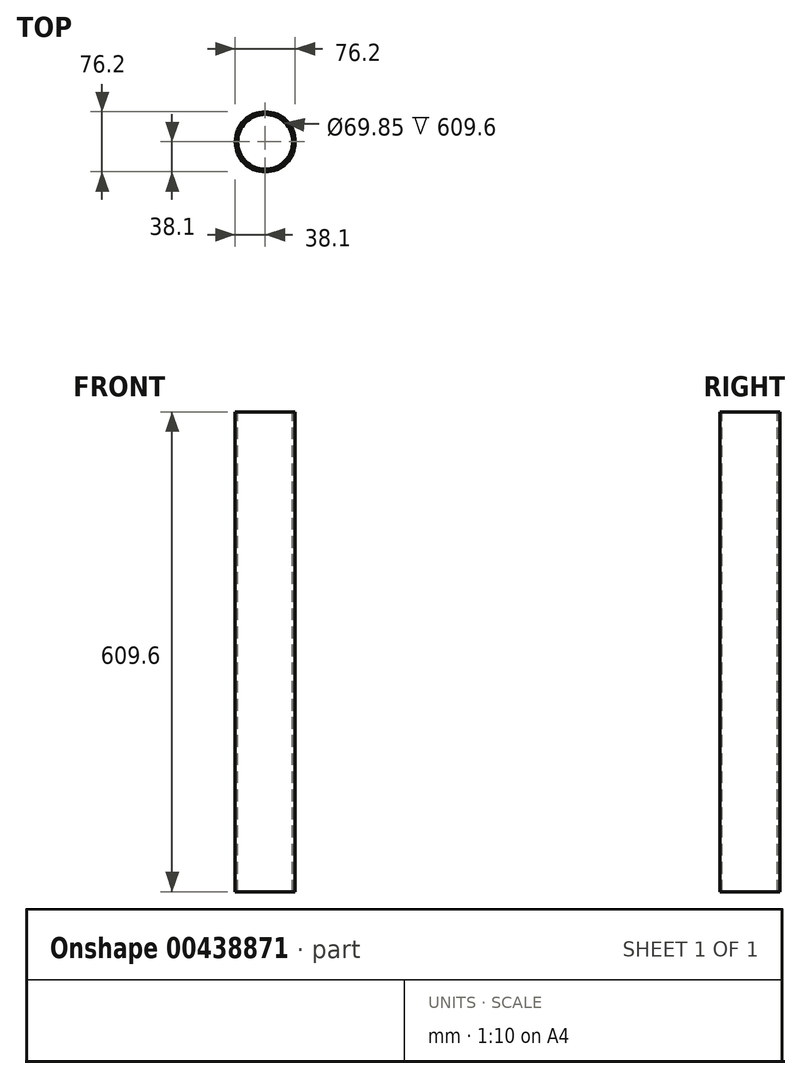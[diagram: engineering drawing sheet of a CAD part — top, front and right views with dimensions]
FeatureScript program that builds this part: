
annotation { "Feature Type Name" : "Feature", "Feature Type Description" : "" }
export const myFeature = defineFeature(function(context is Context, id is Id, definition is map)
    precondition{}
    {
        {
            var Q0;
            Q0=qCreatedBy(makeId("Top.planeOp"),FACE);
            var sketch = newSketch(context, id + "F0", { "sketchPlane" : qUnion([Q0])});
            skCircle(sketch, "E0", {"center": v(0, 0) * mm, "radius": 38.1 * mm});
            skCircle(sketch, "E1", {"center": v(0, 0) * mm, "radius": 34.93 * mm});
            skSolve(sketch);
        }
        {
            var Q0;
            Q0 = qSketchRegion(id + "F0", true);
            extrude(context, id + "F1", {"entities" : qUnion([Q0]), "oppositeDirection" : true, "depth" : 609.6 * mm});
        }
    });
